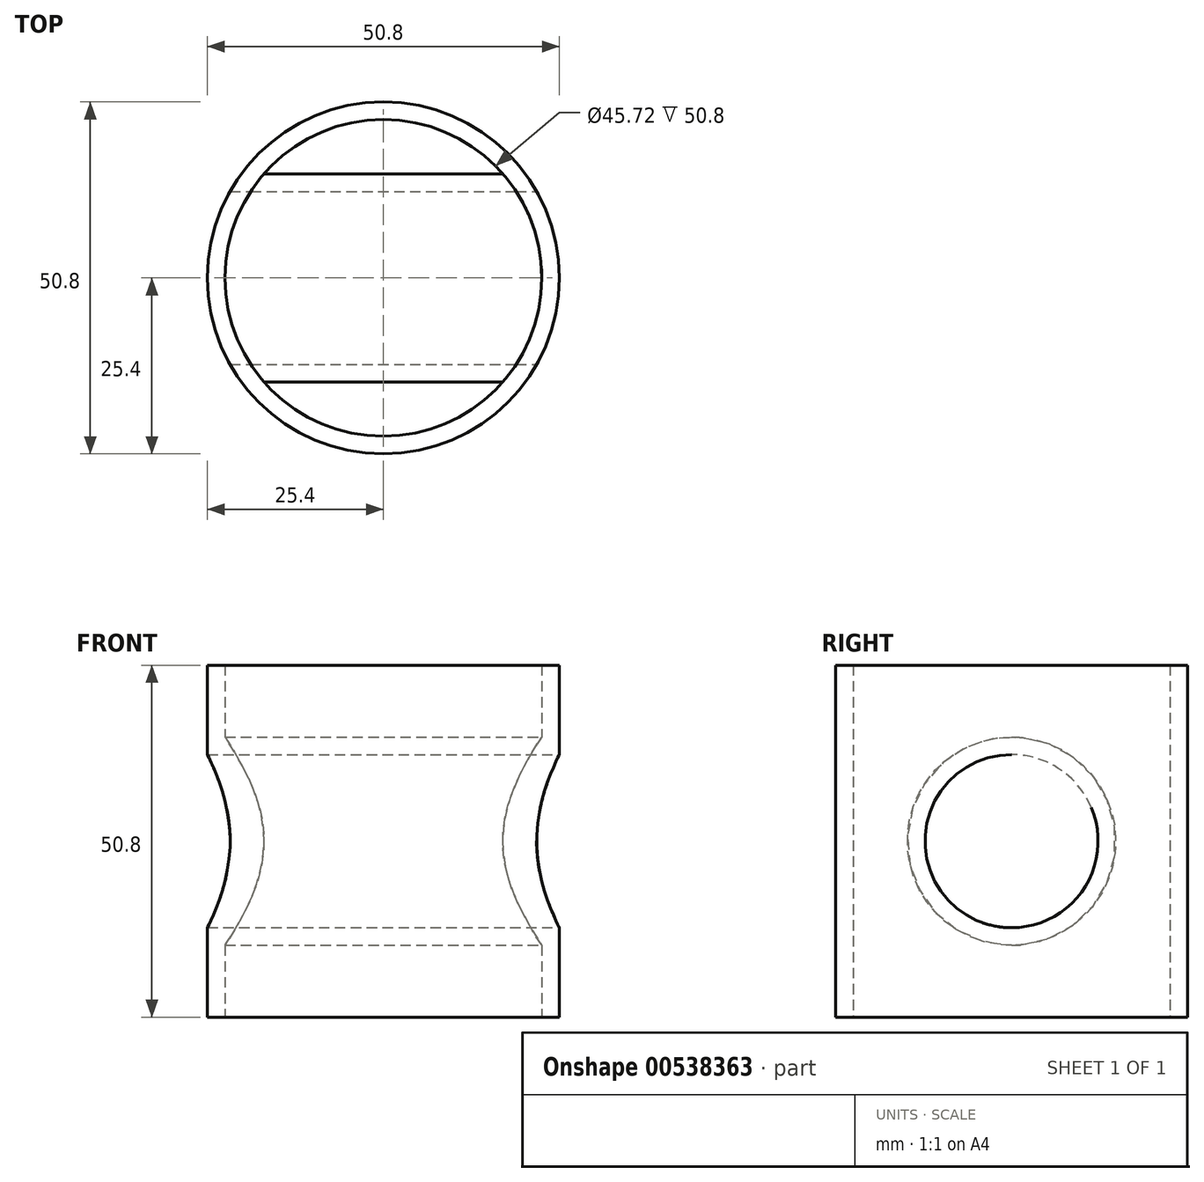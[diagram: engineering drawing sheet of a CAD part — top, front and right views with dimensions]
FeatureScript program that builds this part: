
annotation { "Feature Type Name" : "Feature", "Feature Type Description" : "" }
export const myFeature = defineFeature(function(context is Context, id is Id, definition is map)
    precondition{}
    {
        {
            var Q0;
            Q0=qCreatedBy(makeId("Top.planeOp"),FACE);
            var sketch = newSketch(context, id + "F0", { "sketchPlane" : qUnion([Q0])});
            skCircle(sketch, "E0", {"center": v(0, 0) * mm, "radius": 25.4 * mm});
            skLineSegment(sketch, "E1", {"start": v(0, 0) * mm, "end": v(0, 25.4) * mm, "construction": true});
            skSolve(sketch);
        }
        {
            var Q0;
            Q0 = qSketchRegion(id + "F0", true);
            extrude(context, id + "F1", {"entities" : qUnion([Q0]), "endBound" : BoundingType.SYMMETRIC, "depth" : 50.8 * mm, "offsetDistance" : 25.4 * mm});
        }
        {
            var Q0;
            Q0=qCreatedBy(makeId("Right.planeOp"),FACE);
            var sketch = newSketch(context, id + "F2", { "sketchPlane" : qUnion([Q0])});
            skCircle(sketch, "E2", {"center": v(0, 0) * mm, "radius": 12.5 * mm});
            skSolve(sketch);
        }
        {
            var Q0;
            Q0 = qSketchRegion(id + "F2", true);
            extrude(context, id + "F3", {"entities" : qUnion([Q0]), "operationType" : NewBodyOperationType.REMOVE, "endBound" : BoundingType.SYMMETRIC, "oppositeDirection" : true, "depth" : 86.36 * mm, "offsetDistance" : 25.4 * mm});
        }
        {
            var Q0;
            Q0=makeQuery(id+"F1.opExtrude","CAP_FACE",FACE,{"disambiguationData":[OSD([sQuery(id+"F0.wireOp",EDGE,"E0")])],"isStart":false});
            var Q1;
            Q1=makeQuery(id+"F1.opExtrude","CAP_FACE",FACE,{"disambiguationData":[OSD([sQuery(id+"F0.wireOp",EDGE,"E0")])],"isStart":true});
            shell(context, id + "F4", {"entities" : qUnion([Q0, Q1]), "thickness" : 2.54 * mm});
        }
    });
